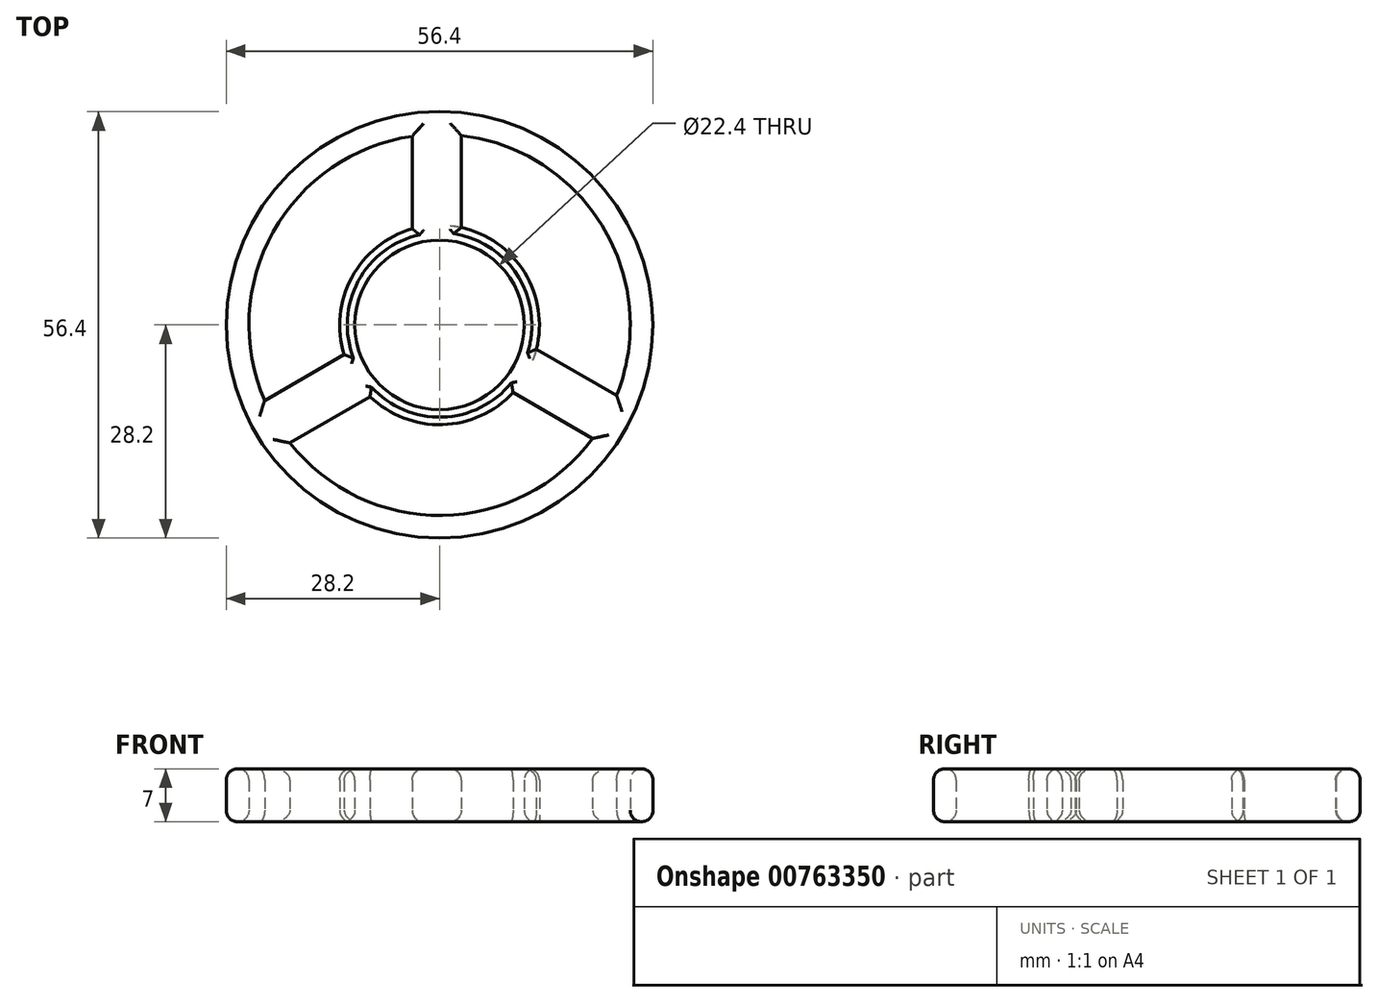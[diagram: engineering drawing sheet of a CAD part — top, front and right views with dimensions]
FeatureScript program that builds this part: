
annotation { "Feature Type Name" : "Feature", "Feature Type Description" : "" }
export const myFeature = defineFeature(function(context is Context, id is Id, definition is map)
    precondition{}
    {
        {
            var Q0;
            Q0=qCreatedBy(makeId("Top.planeOp"),FACE);
            var sketch = newSketch(context, id + "F0", { "sketchPlane" : qUnion([Q0])});
            skCircle(sketch, "E0", {"center": v(0, 0) * mm, "radius": 28.2 * mm});
            skArc(sketch, "E1", {"start": v(-19.79, -15.6) * mm, "mid": v(0.37, -25.2) * mm, "end": v(20.24, -15.02) * mm});
            skCircle(sketch, "E2", {"center": v(0, 0) * mm, "radius": 11.2 * mm});
            skArc(sketch, "E3", {"start": v(-9.18, -9.48) * mm, "mid": v(0.38, -13.2) * mm, "end": v(9.71, -8.94) * mm});
            skLineSegment(sketch, "E4", {"start": v(-3.62, 24.94) * mm, "end": v(-3.62, 12.7) * mm});
            skLineSegment(sketch, "E5", {"start": v(2.89, 25.03) * mm, "end": v(2.89, 12.88) * mm});
            skLineSegment(sketch, "E6.1.0", {"start": v(-19.79, -15.6) * mm, "end": v(-9.18, -9.48) * mm});
            skLineSegment(sketch, "E6.1.1", {"start": v(-23.12, -10.02) * mm, "end": v(-12.6, -3.94) * mm});
            skLineSegment(sketch, "E6.2.0", {"start": v(23.4, -9.34) * mm, "end": v(12.8, -3.21) * mm});
            skLineSegment(sketch, "E6.2.1", {"start": v(20.24, -15.02) * mm, "end": v(9.71, -8.94) * mm});
            skArc(sketch, "E7.trimOffspring", {"start": v(12.8, -3.21) * mm, "mid": v(11.24, 6.92) * mm, "end": v(2.89, 12.88) * mm});
            skArc(sketch, "E8.trimOffspring", {"start": v(23.4, -9.34) * mm, "mid": v(-0.37, 25.2) * mm, "end": v(-23.12, -10.02) * mm});
            skArc(sketch, "E9.trimOffspring", {"start": v(-3.62, 12.7) * mm, "mid": v(-11.62, 6.27) * mm, "end": v(-12.6, -3.94) * mm});
            skSolve(sketch);
        }
        {
            var Q0;
            Q0=makeQuery(id+"F0.imprint","IMPRINT",FACE,{"disambiguationData":[TD([[makeQuery(id+"F0.imprint","IMPRINT",EDGE,{"derivedFrom":sQuery(id+"F0.wireOp",EDGE,"E0")}),1.0]])]});
            extrude(context, id + "F1", {"entities" : qUnion([Q0]), "depth" : 7 * mm, "offsetDistance" : 25 * mm});
        }
        {
            var Q0;
            Q0=makeQuery(id+"F1.opExtrude","CAP_FACE",FACE,{"disambiguationData":[OSD([sQuery(id+"F0.wireOp",EDGE,"E0"),sQuery(id+"F0.wireOp",EDGE,"E1"),sQuery(id+"F0.wireOp",EDGE,"E2"),sQuery(id+"F0.wireOp",EDGE,"E3"),sQuery(id+"F0.wireOp",EDGE,"E4"),sQuery(id+"F0.wireOp",EDGE,"E5"),sQuery(id+"F0.wireOp",EDGE,"E6.1.0"),sQuery(id+"F0.wireOp",EDGE,"E6.1.1"),sQuery(id+"F0.wireOp",EDGE,"E6.2.0"),sQuery(id+"F0.wireOp",EDGE,"E6.2.1"),sQuery(id+"F0.wireOp",EDGE,"E7.trimOffspring"),sQuery(id+"F0.wireOp",EDGE,"E8.trimOffspring"),sQuery(id+"F0.wireOp",EDGE,"E9.trimOffspring")])],"isStart":false});
            var Q1;
            Q1=makeQuery(id+"F1.opExtrude","CAP_EDGE",EDGE,{"disambiguationData":[OSD([sQuery(id+"F0.wireOp",EDGE,"E0")])],"isStart":true});
            var Q2;
            Q2=makeQuery(id+"F1.opExtrude","CAP_EDGE",EDGE,{"disambiguationData":[OSD([sQuery(id+"F0.wireOp",EDGE,"E1")])],"isStart":true});
            var Q3;
            {var subQ0=sQuery(id+"F0.wireOp",EDGE,"E8.trimOffspring");Q3=makeQuery(id+"F1.opExtrude","CAP_EDGE",EDGE,{"disambiguationData":[OSD([subQ0]),TDD([makeQuery(id+"F0.imprint","IMPRINT",EDGE,{"disambiguationData":[TD([[makeQuery(id+"F0.imprint","INTERSECT",VERTEX,{"derivedFrom":[sQuery(id+"F0.wireOp",EDGE,"E4"),subQ0]}),-1.0]])],"derivedFrom":subQ0})])],"isStart":true});}
            var Q4;
            {var subQ0=sQuery(id+"F0.wireOp",EDGE,"E8.trimOffspring");Q4=makeQuery(id+"F1.opExtrude","CAP_EDGE",EDGE,{"disambiguationData":[OSD([subQ0]),TDD([makeQuery(id+"F0.imprint","IMPRINT",EDGE,{"disambiguationData":[TD([[makeQuery(id+"F0.imprint","INTERSECT",VERTEX,{"derivedFrom":[sQuery(id+"F0.wireOp",EDGE,"E5"),subQ0]}),1.0]])],"derivedFrom":subQ0})])],"isStart":true});}
            var Q5;
            Q5=makeQuery(id+"F1.opExtrude","CAP_EDGE",EDGE,{"disambiguationData":[OSD([sQuery(id+"F0.wireOp",EDGE,"E5")])],"isStart":true});
            var Q6;
            Q6=makeQuery(id+"F1.opExtrude","CAP_EDGE",EDGE,{"disambiguationData":[OSD([sQuery(id+"F0.wireOp",EDGE,"E6.2.0")])],"isStart":true});
            var Q7;
            Q7=makeQuery(id+"F1.opExtrude","CAP_EDGE",EDGE,{"disambiguationData":[OSD([sQuery(id+"F0.wireOp",EDGE,"E6.2.1")])],"isStart":true});
            var Q8;
            Q8=makeQuery(id+"F1.opExtrude","CAP_EDGE",EDGE,{"disambiguationData":[OSD([sQuery(id+"F0.wireOp",EDGE,"E3")])],"isStart":true});
            var Q9;
            Q9=makeQuery(id+"F1.opExtrude","CAP_EDGE",EDGE,{"disambiguationData":[OSD([sQuery(id+"F0.wireOp",EDGE,"E6.1.0")])],"isStart":true});
            var Q10;
            Q10=makeQuery(id+"F1.opExtrude","CAP_EDGE",EDGE,{"disambiguationData":[OSD([sQuery(id+"F0.wireOp",EDGE,"E6.1.1")])],"isStart":true});
            var Q11;
            Q11=makeQuery(id+"F1.opExtrude","CAP_EDGE",EDGE,{"disambiguationData":[OSD([sQuery(id+"F0.wireOp",EDGE,"E9.trimOffspring")])],"isStart":true});
            var Q12;
            Q12=makeQuery(id+"F1.opExtrude","CAP_EDGE",EDGE,{"disambiguationData":[OSD([sQuery(id+"F0.wireOp",EDGE,"E4")])],"isStart":true});
            var Q13;
            Q13=makeQuery(id+"F1.opExtrude","CAP_EDGE",EDGE,{"disambiguationData":[OSD([sQuery(id+"F0.wireOp",EDGE,"E2")])],"isStart":true});
            fillet(context, id + "F2", {"entities" : qUnion([Q0, Q1, Q2, Q3, Q4, Q5, Q6, Q7, Q8, Q9, Q10, Q11, Q12, Q13]), "radius" : 1.5 * mm, "tangentPropagation" : true, "allowEdgeOverflow" : false});
        }
    });
